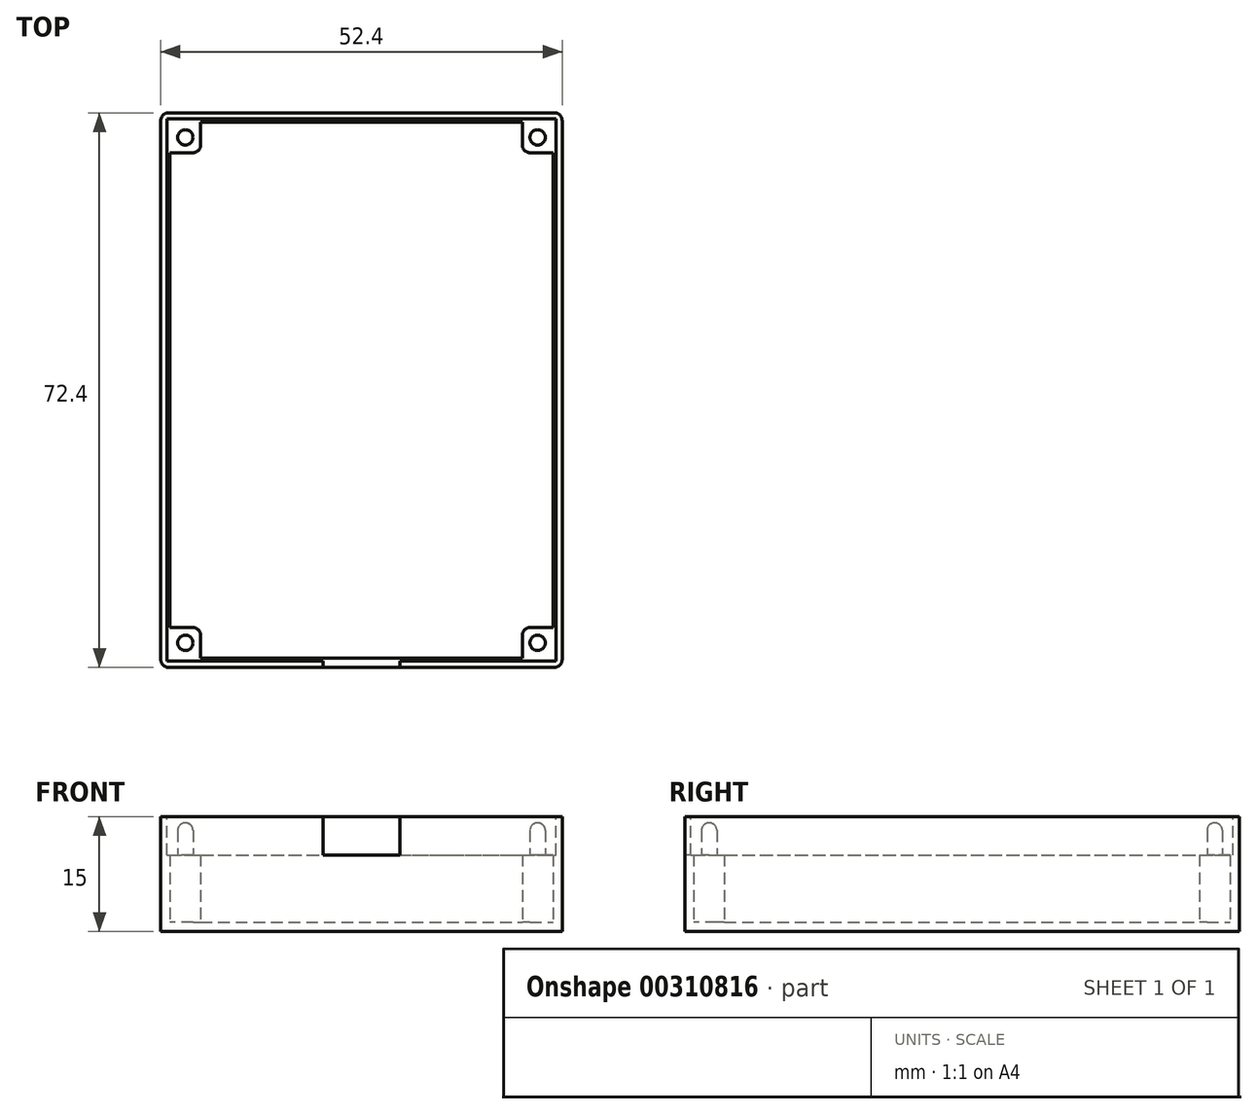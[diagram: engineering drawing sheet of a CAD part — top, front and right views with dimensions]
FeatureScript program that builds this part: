
annotation { "Feature Type Name" : "Feature", "Feature Type Description" : "" }
export const myFeature = defineFeature(function(context is Context, id is Id, definition is map)
    precondition{}
    {
        {
            var Q0;
            Q0=qCreatedBy(makeId("Top.planeOp"),FACE);
            var sketch = newSketch(context, id + "F0", { "sketchPlane" : qUnion([Q0])});
            skLineSegment(sketch, "E0.bottom", {"start": v(0, 0) * mm, "end": v(50, 0) * mm, "construction": true});
            skLineSegment(sketch, "E0.top", {"start": v(0, 70) * mm, "end": v(50, 70) * mm, "construction": true});
            skLineSegment(sketch, "E0.left", {"start": v(0, 0) * mm, "end": v(0, 70) * mm, "construction": true});
            skLineSegment(sketch, "E0.right", {"start": v(50, 0) * mm, "end": v(50, 70) * mm, "construction": true});
            skLineSegment(sketch, "E1", {"start": v(25, 70) * mm, "end": v(25, 0) * mm, "construction": true});
            skLineSegment(sketch, "E2", {"start": v(0, 35) * mm, "end": v(50, 35) * mm, "construction": true});
            skCircle(sketch, "E3", {"center": v(2, 68) * mm, "radius": 1 * mm});
            skCircle(sketch, "E4.MirrorC", {"center": v(48, 68) * mm, "radius": 1 * mm});
            skCircle(sketch, "E5.MirrorC", {"center": v(2, 2) * mm, "radius": 1 * mm});
            skCircle(sketch, "E6.MirrorC", {"center": v(48, 2) * mm, "radius": 1 * mm});
            skLineSegment(sketch, "E7.bottom", {"start": v(0, 70) * mm, "end": v(4, 70) * mm});
            skLineSegment(sketch, "E7.top", {"start": v(0, 66) * mm, "end": v(3, 66) * mm});
            skLineSegment(sketch, "E7.left", {"start": v(0, 70) * mm, "end": v(0, 66) * mm});
            skLineSegment(sketch, "E7.right", {"start": v(4, 70) * mm, "end": v(4, 67) * mm});
            skPoint(sketch, "E8.visualSharp", {"position": v(4, 66) * mm});
            skArc(sketch, "E8.filletArc", {"start": v(3, 66) * mm, "mid": v(3.7, 66.3) * mm, "end": v(4, 67) * mm});
            skLineSegment(sketch, "E9.MirrorCS", {"start": v(50, 66) * mm, "end": v(47, 66) * mm});
            skPoint(sketch, "E10.MirrorP", {"position": v(46, 66) * mm});
            skArc(sketch, "E11.MirrorCS", {"start": v(47, 66) * mm, "mid": v(46.3, 66.3) * mm, "end": v(46, 67) * mm});
            skLineSegment(sketch, "E12.MirrorCS", {"start": v(46, 70) * mm, "end": v(46, 67) * mm});
            skLineSegment(sketch, "E13", {"start": v(46, 70) * mm, "end": v(50, 70) * mm});
            skLineSegment(sketch, "E14", {"start": v(50, 66) * mm, "end": v(50, 70) * mm});
            skLineSegment(sketch, "E15.MirrorCS", {"start": v(50, 4) * mm, "end": v(47, 4) * mm});
            skArc(sketch, "E16.MirrorCS", {"start": v(47, 4) * mm, "mid": v(46.3, 3.7) * mm, "end": v(46, 3) * mm});
            skLineSegment(sketch, "E17.MirrorCS", {"start": v(46, 0) * mm, "end": v(46, 3) * mm});
            skArc(sketch, "E18.MirrorCS", {"start": v(3, 4) * mm, "mid": v(3.7, 3.7) * mm, "end": v(4, 3) * mm});
            skLineSegment(sketch, "E19.MirrorCS", {"start": v(0, 4) * mm, "end": v(3, 4) * mm});
            skLineSegment(sketch, "E20.MirrorCS", {"start": v(4, 0) * mm, "end": v(4, 3) * mm});
            skLineSegment(sketch, "E21", {"start": v(4, 0) * mm, "end": v(0, 0) * mm});
            skLineSegment(sketch, "E22", {"start": v(0, 0) * mm, "end": v(0, 4) * mm});
            skLineSegment(sketch, "E23", {"start": v(50, 0) * mm, "end": v(46, 0) * mm});
            skLineSegment(sketch, "E24", {"start": v(50, 4) * mm, "end": v(50, 0) * mm});
            skSolve(sketch);
        }
        {
            var Q0;
            Q0=qCreatedBy(makeId("Top.planeOp"),FACE);
            var sketch = newSketch(context, id + "F1", { "sketchPlane" : qUnion([Q0])});
            skLineSegment(sketch, "E25.0", {"start": v(51.2, -1.2) * mm, "end": v(51.2, 71.2) * mm});
            skLineSegment(sketch, "E25.1", {"start": v(-1.2, -1.2) * mm, "end": v(51.2, -1.2) * mm});
            skLineSegment(sketch, "E25.2", {"start": v(-1.2, -1.2) * mm, "end": v(-1.2, 71.2) * mm});
            skLineSegment(sketch, "E25.3", {"start": v(-1.2, 71.2) * mm, "end": v(51.2, 71.2) * mm});
            skSolve(sketch);
        }
        {
            var Q0;
            Q0 = qSketchRegion(id + "F1", true);
            extrude(context, id + "F2", {"entities" : qUnion([Q0]), "depth" : 15 * mm});
        }
        {
            var Q0;
            Q0=makeQuery(id+"F2.opExtrude","CAP_FACE",FACE,{"disambiguationData":[OSD([sQuery(id+"F1.wireOp",EDGE,"E25.0"),sQuery(id+"F1.wireOp",EDGE,"E25.1"),sQuery(id+"F1.wireOp",EDGE,"E25.2"),sQuery(id+"F1.wireOp",EDGE,"E25.3")])],"isStart":false});
            shell(context, id + "F3", {"entities" : qUnion([Q0]), "thickness" : 1.2 * mm});
        }
        {
            var Q0;
            Q0 = qSketchRegion(id + "F0", true);
            extrude(context, id + "F4", {"entities" : qUnion([Q0]), "operationType" : NewBodyOperationType.ADD, "depth" : 10 * mm});
        }
        {
            var Q0;
            Q0=makeQuery(id+"F4.boolean.opBoolean","SPLIT",FACE,{"disambiguationData":[TD([makeQuery(id+"F4.opExtrude","SWEPT_FACE",FACE,{"disambiguationData":[OSD([sQuery(id+"F0.wireOp",EDGE,"E5.MirrorC")])]})])],"derivedFrom":makeQuery(id+"F3.opShell","OFFSET_FACE",FACE,{"disambiguationData":[OSD([sQuery(id+"F1.wireOp",EDGE,"E25.0"),sQuery(id+"F1.wireOp",EDGE,"E25.1"),sQuery(id+"F1.wireOp",EDGE,"E25.2"),sQuery(id+"F1.wireOp",EDGE,"E25.3")])]})});
            var Q1;
            Q1=makeQuery(id+"F4.boolean.opBoolean","SPLIT",FACE,{"disambiguationData":[TD([makeQuery(id+"F4.opExtrude","SWEPT_FACE",FACE,{"disambiguationData":[OSD([sQuery(id+"F0.wireOp",EDGE,"E6.MirrorC")])]})])],"derivedFrom":makeQuery(id+"F3.opShell","OFFSET_FACE",FACE,{"disambiguationData":[OSD([sQuery(id+"F1.wireOp",EDGE,"E25.0"),sQuery(id+"F1.wireOp",EDGE,"E25.1"),sQuery(id+"F1.wireOp",EDGE,"E25.2"),sQuery(id+"F1.wireOp",EDGE,"E25.3")])]})});
            var Q2;
            Q2=makeQuery(id+"F4.boolean.opBoolean","SPLIT",FACE,{"disambiguationData":[TD([makeQuery(id+"F4.opExtrude","SWEPT_FACE",FACE,{"disambiguationData":[OSD([sQuery(id+"F0.wireOp",EDGE,"E3")])]})])],"derivedFrom":makeQuery(id+"F3.opShell","OFFSET_FACE",FACE,{"disambiguationData":[OSD([sQuery(id+"F1.wireOp",EDGE,"E25.0"),sQuery(id+"F1.wireOp",EDGE,"E25.1"),sQuery(id+"F1.wireOp",EDGE,"E25.2"),sQuery(id+"F1.wireOp",EDGE,"E25.3")])]})});
            var Q3;
            Q3=makeQuery(id+"F4.boolean.opBoolean","SPLIT",FACE,{"disambiguationData":[TD([makeQuery(id+"F4.opExtrude","SWEPT_FACE",FACE,{"disambiguationData":[OSD([sQuery(id+"F0.wireOp",EDGE,"E4.MirrorC")])]})])],"derivedFrom":makeQuery(id+"F3.opShell","OFFSET_FACE",FACE,{"disambiguationData":[OSD([sQuery(id+"F1.wireOp",EDGE,"E25.0"),sQuery(id+"F1.wireOp",EDGE,"E25.1"),sQuery(id+"F1.wireOp",EDGE,"E25.2"),sQuery(id+"F1.wireOp",EDGE,"E25.3")])]})});
            extrude(context, id + "F5", {"entities" : qUnion([Q0, Q1, Q2, Q3]), "operationType" : NewBodyOperationType.ADD, "depth" : 13 * mm});
        }
        {
            var Q0;
            {var subQ0=sQuery(id+"F1.wireOp",EDGE,"E25.3");var subQ1=sQuery(id+"F1.wireOp",EDGE,"E25.2");var subQ2=sQuery(id+"F1.wireOp",EDGE,"E25.1");var subQ3=sQuery(id+"F1.wireOp",EDGE,"E25.0");Q0=makeQuery(id+"F5.opExtrude","CAP_FACE",FACE,{"disambiguationData":[OSD([subQ3,subQ2,subQ1,subQ0]),TDD([makeQuery(id+"F4.boolean.opBoolean","SPLIT",FACE,{"disambiguationData":[TD([makeQuery(id+"F4.opExtrude","SWEPT_FACE",FACE,{"disambiguationData":[OSD([sQuery(id+"F0.wireOp",EDGE,"E3")])]})])],"derivedFrom":makeQuery(id+"F3.opShell","OFFSET_FACE",FACE,{"disambiguationData":[OSD([subQ3,subQ2,subQ1,subQ0])]})})])],"isStart":false});}
            var Q1;
            Q1=makeQuery(id+"F5.opExtrude","CAP_EDGE",EDGE,{"disambiguationData":[OSD([sQuery(id+"F0.wireOp",EDGE,"E4.MirrorC"),sQuery(id+"F1.wireOp",EDGE,"E25.0"),sQuery(id+"F1.wireOp",EDGE,"E25.1"),sQuery(id+"F1.wireOp",EDGE,"E25.2"),sQuery(id+"F1.wireOp",EDGE,"E25.3")])],"isStart":false});
            var Q2;
            Q2=makeQuery(id+"F5.opExtrude","CAP_EDGE",EDGE,{"disambiguationData":[OSD([sQuery(id+"F0.wireOp",EDGE,"E3"),sQuery(id+"F1.wireOp",EDGE,"E25.0"),sQuery(id+"F1.wireOp",EDGE,"E25.1"),sQuery(id+"F1.wireOp",EDGE,"E25.2"),sQuery(id+"F1.wireOp",EDGE,"E25.3")])],"isStart":false});
            var Q3;
            Q3=makeQuery(id+"F5.opExtrude","CAP_EDGE",EDGE,{"disambiguationData":[OSD([sQuery(id+"F0.wireOp",EDGE,"E6.MirrorC"),sQuery(id+"F1.wireOp",EDGE,"E25.0"),sQuery(id+"F1.wireOp",EDGE,"E25.1"),sQuery(id+"F1.wireOp",EDGE,"E25.2"),sQuery(id+"F1.wireOp",EDGE,"E25.3")])],"isStart":false});
            var Q4;
            Q4=makeQuery(id+"F5.opExtrude","CAP_EDGE",EDGE,{"disambiguationData":[OSD([sQuery(id+"F0.wireOp",EDGE,"E5.MirrorC"),sQuery(id+"F1.wireOp",EDGE,"E25.0"),sQuery(id+"F1.wireOp",EDGE,"E25.1"),sQuery(id+"F1.wireOp",EDGE,"E25.2"),sQuery(id+"F1.wireOp",EDGE,"E25.3")])],"isStart":false});
            fillet(context, id + "F6", {"entities" : qUnion([Q0, Q1, Q2, Q3, Q4]), "radius" : 1 * mm, "tangentPropagation" : true, "allowEdgeOverflow" : false});
        }
        {
            var Q0;
            Q0=makeQuery(id+"F2.opExtrude","SWEPT_EDGE",EDGE,{"disambiguationData":[OSD([sQuery(id+"F1.wireOp",EDGE,"E25.1"),sQuery(id+"F1.wireOp",EDGE,"E25.2")])]});
            var Q1;
            Q1=makeQuery(id+"F2.opExtrude","SWEPT_EDGE",EDGE,{"disambiguationData":[OSD([sQuery(id+"F1.wireOp",EDGE,"E25.0"),sQuery(id+"F1.wireOp",EDGE,"E25.1")])]});
            var Q2;
            Q2=makeQuery(id+"F2.opExtrude","SWEPT_EDGE",EDGE,{"disambiguationData":[OSD([sQuery(id+"F1.wireOp",EDGE,"E25.2"),sQuery(id+"F1.wireOp",EDGE,"E25.3")])]});
            var Q3;
            Q3=makeQuery(id+"F2.opExtrude","SWEPT_EDGE",EDGE,{"disambiguationData":[OSD([sQuery(id+"F1.wireOp",EDGE,"E25.0"),sQuery(id+"F1.wireOp",EDGE,"E25.3")])]});
            fillet(context, id + "F7", {"entities" : qUnion([Q0, Q1, Q2, Q3]), "radius" : 1 * mm, "tangentPropagation" : true, "allowEdgeOverflow" : false});
        }
        {
            var Q0;
            Q0=makeQuery(id+"F2.opExtrude","CAP_FACE",FACE,{"disambiguationData":[OSD([sQuery(id+"F1.wireOp",EDGE,"E25.0"),sQuery(id+"F1.wireOp",EDGE,"E25.1"),sQuery(id+"F1.wireOp",EDGE,"E25.2"),sQuery(id+"F1.wireOp",EDGE,"E25.3")])],"isStart":false});
            var sketch = newSketch(context, id + "F8", { "sketchPlane" : qUnion([Q0])});
            skLineSegment(sketch, "E26.0", {"start": v(-0.4, 70.4) * mm, "end": v(50.4, 70.4) * mm});
            skLineSegment(sketch, "E26.1", {"start": v(-0.4, -0.4) * mm, "end": v(-0.4, 70.4) * mm});
            skLineSegment(sketch, "E26.2", {"start": v(-0.4, -0.4) * mm, "end": v(50.4, -0.4) * mm});
            skLineSegment(sketch, "E26.3", {"start": v(50.4, -0.4) * mm, "end": v(50.4, 70.4) * mm});
            skLineSegment(sketch, "E27.0", {"start": v(0, 0) * mm, "end": v(50, 0) * mm});
            skLineSegment(sketch, "E27.1", {"start": v(0, 0) * mm, "end": v(0, 70) * mm});
            skLineSegment(sketch, "E27.2", {"start": v(0, 70) * mm, "end": v(50, 70) * mm});
            skLineSegment(sketch, "E27.3", {"start": v(50, 0) * mm, "end": v(50, 70) * mm});
            skSolve(sketch);
        }
        {
            var Q0;
            Q0 = qSketchRegion(id + "F8", true);
            extrude(context, id + "F9", {"entities" : qUnion([Q0]), "operationType" : NewBodyOperationType.REMOVE, "oppositeDirection" : true, "depth" : 5 * mm});
        }
        {
            var Q0;
            Q0=makeQuery(id+"F2.opExtrude","SWEPT_FACE",FACE,{"disambiguationData":[OSD([sQuery(id+"F1.wireOp",EDGE,"E25.1")])]});
            var sketch = newSketch(context, id + "F10", { "sketchPlane" : qUnion([Q0])});
            skLineSegment(sketch, "E28.bottom", {"start": v(30, 10) * mm, "end": v(20, 10) * mm});
            skLineSegment(sketch, "E28.top", {"start": v(30, 20) * mm, "end": v(20, 20) * mm});
            skLineSegment(sketch, "E28.left", {"start": v(30, 10) * mm, "end": v(30, 20) * mm});
            skLineSegment(sketch, "E28.right", {"start": v(20, 10) * mm, "end": v(20, 20) * mm});
            skPoint(sketch, "E28.middle", {"position": v(25, 15) * mm});
            skSolve(sketch);
        }
        {
            var Q0;
            Q0 = qSketchRegion(id + "F10", true);
            extrude(context, id + "F11", {"entities" : qUnion([Q0]), "operationType" : NewBodyOperationType.REMOVE, "oppositeDirection" : true, "depth" : 25 * mm});
        }
    });
